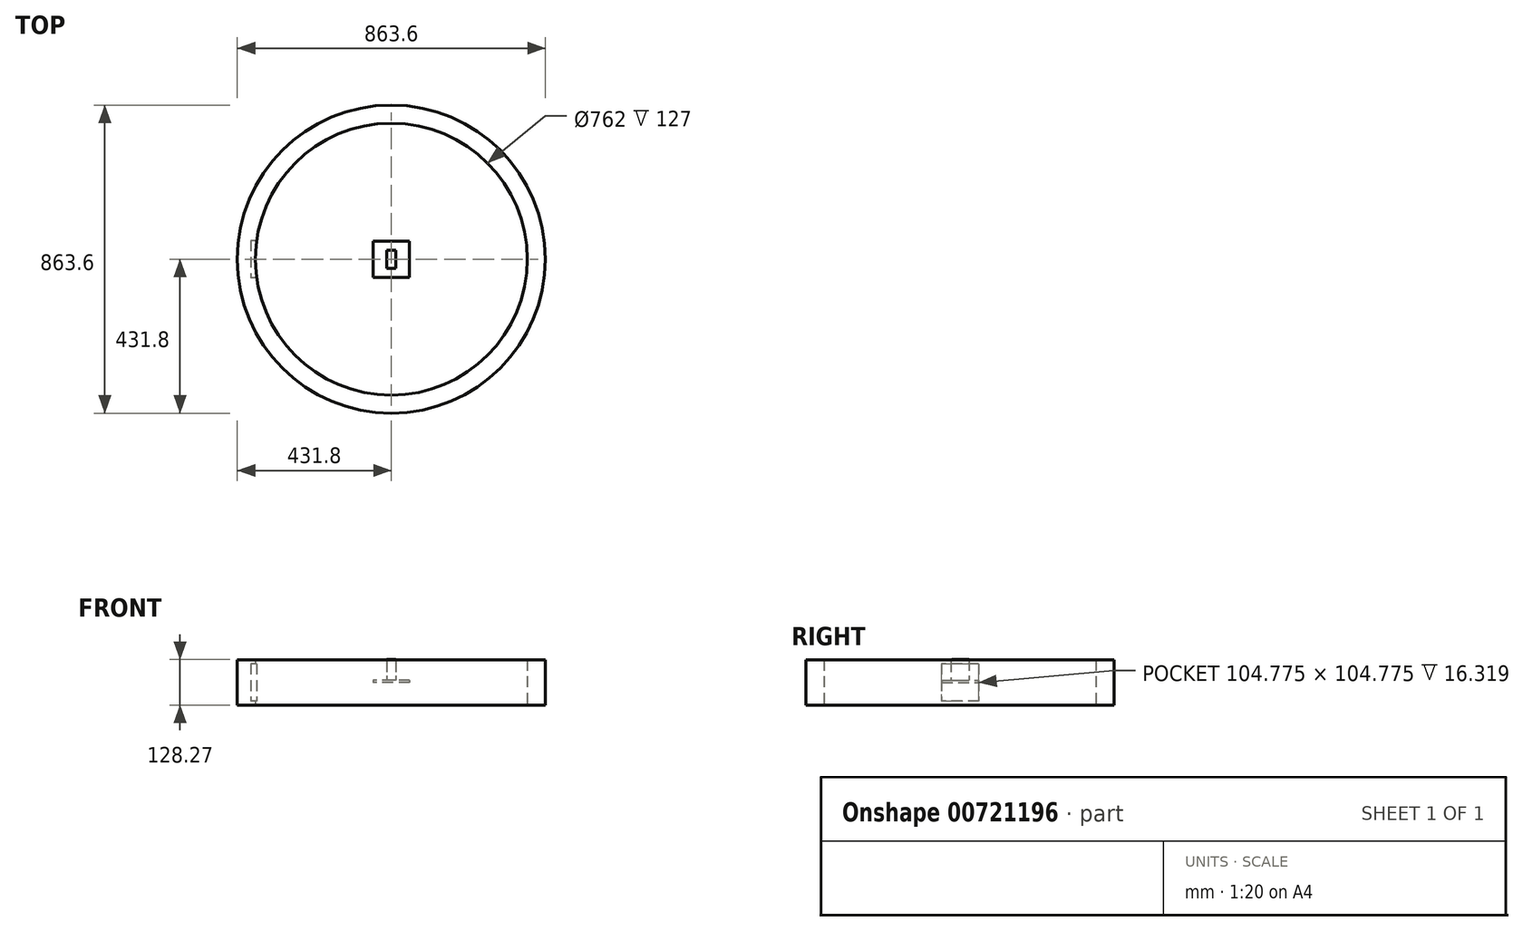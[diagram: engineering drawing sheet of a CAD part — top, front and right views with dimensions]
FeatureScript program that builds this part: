
annotation { "Feature Type Name" : "Feature", "Feature Type Description" : "" }
export const myFeature = defineFeature(function(context is Context, id is Id, definition is map)
    precondition{}
    {
        {
            var Q0;
            Q0=qCreatedBy(makeId("Top.planeOp"),FACE);
            var sketch = newSketch(context, id + "F0", { "sketchPlane" : qUnion([Q0])});
            skCircle(sketch, "E0", {"center": v(0, 0) * mm, "radius": 431.8 * mm});
            skCircle(sketch, "E1", {"center": v(0, 0) * mm, "radius": 381 * mm});
            skSolve(sketch);
        }
        {
            var Q0;
            Q0 = qSketchRegion(id + "F0", true);
            extrude(context, id + "F1", {"entities" : qUnion([Q0]), "depth" : 127 * mm, "offsetDistance" : 25.4 * mm, "symmetric" : true});
        }
        {
            var Q0;
            Q0=qCreatedBy(makeId("Front.planeOp"),FACE);
            var sketch = newSketch(context, id + "F2", { "sketchPlane" : qUnion([Q0])});
            skLineSegment(sketch, "E2.bottom", {"start": v(-342.9, 52.39) * mm, "end": v(-393.7, 52.39) * mm});
            skLineSegment(sketch, "E2.top", {"start": v(-342.9, -52.39) * mm, "end": v(-393.7, -52.39) * mm});
            skLineSegment(sketch, "E2.left", {"start": v(-342.9, 52.39) * mm, "end": v(-342.9, -52.39) * mm});
            skLineSegment(sketch, "E2.right", {"start": v(-393.7, 52.39) * mm, "end": v(-393.7, -52.39) * mm});
            skLineSegment(sketch, "E3", {"start": v(0, 0) * mm, "end": v(-342.9, 0) * mm, "construction": true});
            skSolve(sketch);
        }
        {
            var Q0;
            Q0 = qSketchRegion(id + "F2", true);
            extrude(context, id + "F3", {"entities" : qUnion([Q0]), "operationType" : NewBodyOperationType.REMOVE, "oppositeDirection" : true, "depth" : 104.77 * mm, "offsetDistance" : 25.4 * mm, "symmetric" : true});
        }
        {
            var Q0;
            Q0=qCreatedBy(makeId("Top.planeOp"),FACE);
            var sketch = newSketch(context, id + "F4", { "sketchPlane" : qUnion([Q0])});
            skLineSegment(sketch, "E4.bottom", {"start": v(50.8, -50.8) * mm, "end": v(-50.8, -50.8) * mm});
            skLineSegment(sketch, "E4.top", {"start": v(50.8, 50.8) * mm, "end": v(-50.8, 50.8) * mm});
            skLineSegment(sketch, "E4.left", {"start": v(50.8, -50.8) * mm, "end": v(50.8, 50.8) * mm});
            skLineSegment(sketch, "E4.right", {"start": v(-50.8, -50.8) * mm, "end": v(-50.8, 50.8) * mm});
            skPoint(sketch, "E4.middle", {"position": v(0, 0) * mm});
            skSolve(sketch);
        }
        {
            var Q0;
            Q0 = qSketchRegion(id + "F4", true);
            extrude(context, id + "F5", {"entities" : qUnion([Q0]), "depth" : 6.35 * mm, "offsetDistance" : 25.4 * mm});
        }
        {
            var Q0;
            Q0=makeQuery(id+"F5.opExtrude","CAP_FACE",FACE,{"disambiguationData":[OSD([sQuery(id+"F4.wireOp",EDGE,"E4.bottom"),sQuery(id+"F4.wireOp",EDGE,"E4.top"),sQuery(id+"F4.wireOp",EDGE,"E4.left"),sQuery(id+"F4.wireOp",EDGE,"E4.right")])],"isStart":false});
            var sketch = newSketch(context, id + "F6", { "sketchPlane" : qUnion([Q0])});
            skLineSegment(sketch, "E5.bottom", {"start": v(12.7, -25.4) * mm, "end": v(-12.7, -25.4) * mm});
            skLineSegment(sketch, "E5.top", {"start": v(12.7, 25.4) * mm, "end": v(-12.7, 25.4) * mm});
            skLineSegment(sketch, "E5.left", {"start": v(12.7, -25.4) * mm, "end": v(12.7, 25.4) * mm});
            skLineSegment(sketch, "E5.right", {"start": v(-12.7, -25.4) * mm, "end": v(-12.7, 25.4) * mm});
            skPoint(sketch, "E5.middle", {"position": v(0, 0) * mm});
            skSolve(sketch);
        }
        {
            var Q0;
            Q0 = qSketchRegion(id + "F6", true);
            extrude(context, id + "F7", {"entities" : qUnion([Q0]), "operationType" : NewBodyOperationType.ADD, "depth" : 58.42 * mm, "offsetDistance" : 25.4 * mm});
        }
        {
            var Q0;
            Q0=makeQuery(id+"F7.opExtrude","CAP_EDGE",EDGE,{"disambiguationData":[OSD([sQuery(id+"F6.wireOp",EDGE,"E5.bottom")])],"isStart":false});
            fillet(context, id + "F8", {"entities" : qUnion([Q0]), "radius" : 5.08 * mm, "tangentPropagation" : true, "allowEdgeOverflow" : false});
        }
    });
